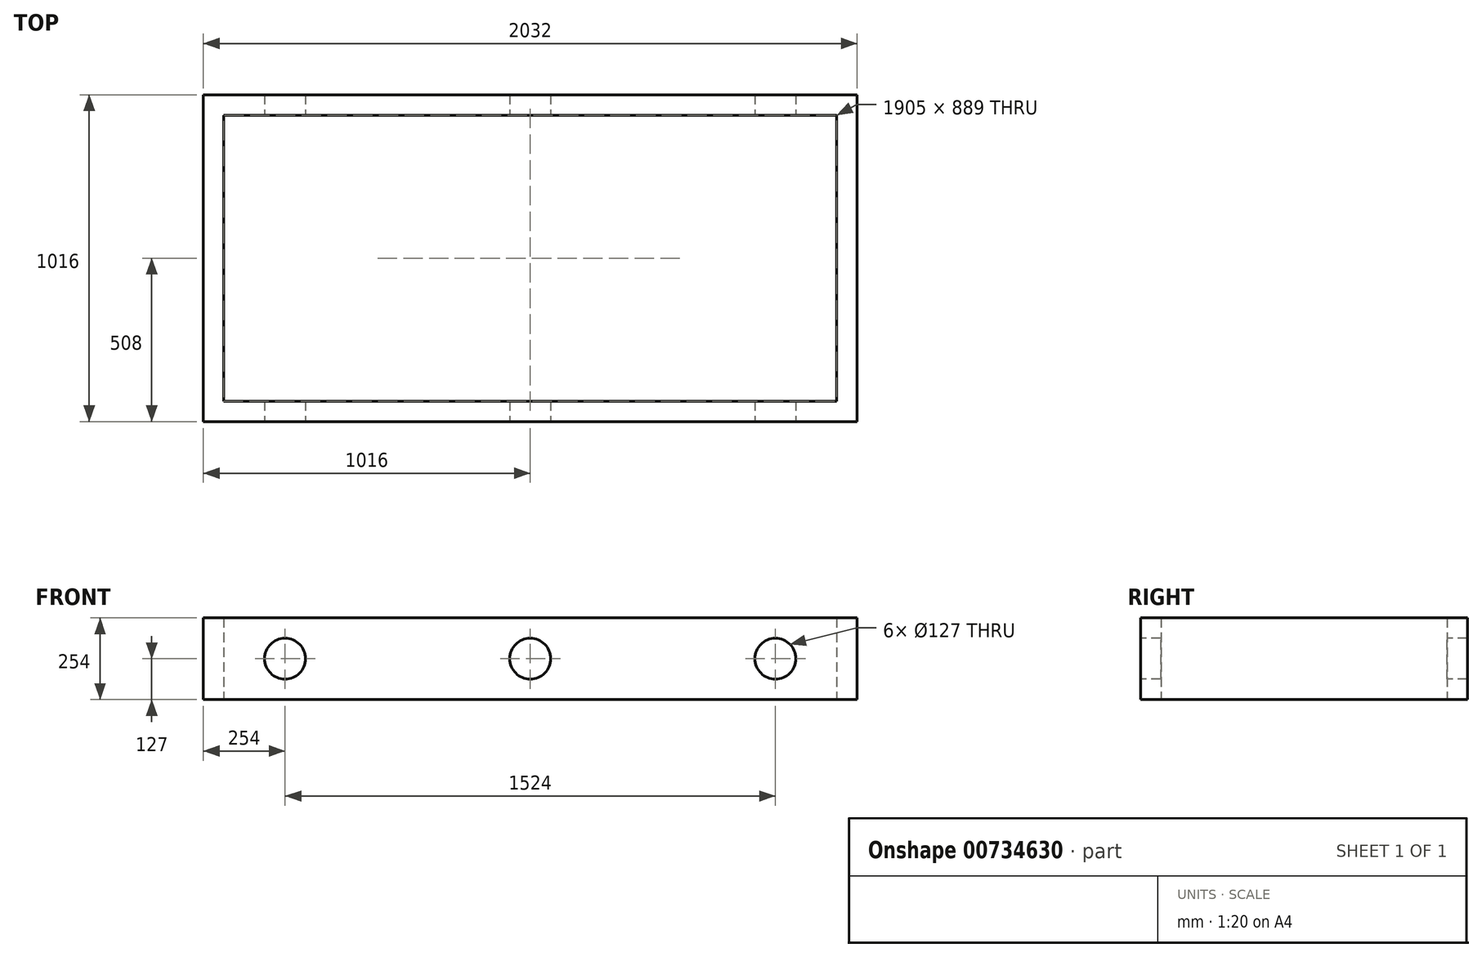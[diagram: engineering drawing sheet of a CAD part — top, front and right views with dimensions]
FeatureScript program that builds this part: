
annotation { "Feature Type Name" : "Feature", "Feature Type Description" : "" }
export const myFeature = defineFeature(function(context is Context, id is Id, definition is map)
    precondition{}
    {
        {
            var Q0;
            Q0=qCreatedBy(makeId("Top.planeOp"),FACE);
            var sketch = newSketch(context, id + "F0", { "sketchPlane" : qUnion([Q0])});
            skLineSegment(sketch, "E0.bottom", {"start": v(1016, -508) * mm, "end": v(-1016, -508) * mm});
            skLineSegment(sketch, "E0.top", {"start": v(1016, 508) * mm, "end": v(-1016, 508) * mm});
            skLineSegment(sketch, "E0.left", {"start": v(1016, -508) * mm, "end": v(1016, 508) * mm});
            skLineSegment(sketch, "E0.right", {"start": v(-1016, -508) * mm, "end": v(-1016, 508) * mm});
            skPoint(sketch, "E0.middle", {"position": v(0, 0) * mm});
            skLineSegment(sketch, "E1.0", {"start": v(952.5, 444.5) * mm, "end": v(-952.5, 444.5) * mm});
            skLineSegment(sketch, "E1.1", {"start": v(952.5, -444.5) * mm, "end": v(952.5, 444.5) * mm});
            skLineSegment(sketch, "E1.2", {"start": v(952.5, -444.5) * mm, "end": v(-952.5, -444.5) * mm});
            skLineSegment(sketch, "E1.3", {"start": v(-952.5, -444.5) * mm, "end": v(-952.5, 444.5) * mm});
            skSolve(sketch);
        }
        {
            var Q0;
            Q0=makeQuery(id+"F0.imprint","IMPRINT",FACE,{"disambiguationData":[TD([[makeQuery(id+"F0.imprint","IMPRINT",EDGE,{"derivedFrom":sQuery(id+"F0.wireOp",EDGE,"E0.bottom")}),-1.0]])]});
            extrude(context, id + "F1", {"entities" : qUnion([Q0]), "depth" : 254 * mm, "offsetDistance" : 25.4 * mm});
        }
        {
            var Q0;
            Q0=makeQuery(id+"F1.opExtrude","SWEPT_FACE",FACE,{"disambiguationData":[OSD([sQuery(id+"F0.wireOp",EDGE,"E0.bottom")])]});
            var sketch = newSketch(context, id + "F2", { "sketchPlane" : qUnion([Q0])});
            skLineSegment(sketch, "E2", {"start": v(-762, 127) * mm, "end": v(762, 127) * mm, "construction": true});
            skCircle(sketch, "E3", {"center": v(-762, 127) * mm, "radius": 63.5 * mm});
            skCircle(sketch, "E4", {"center": v(0, 127) * mm, "radius": 63.5 * mm});
            skCircle(sketch, "E5", {"center": v(762, 127) * mm, "radius": 63.5 * mm});
            skSolve(sketch);
        }
        {
            var Q0;
            Q0=makeQuery(id+"F2.imprint","IMPRINT",FACE,{"disambiguationData":[TD([[makeQuery(id+"F2.imprint","IMPRINT",EDGE,{"derivedFrom":sQuery(id+"F2.wireOp",EDGE,"E4")}),1.0]])]});
            var Q1;
            Q1=makeQuery(id+"F2.imprint","IMPRINT",FACE,{"disambiguationData":[TD([[makeQuery(id+"F2.imprint","IMPRINT",EDGE,{"derivedFrom":sQuery(id+"F2.wireOp",EDGE,"E5")}),1.0]])]});
            var Q2;
            Q2=makeQuery(id+"F2.imprint","IMPRINT",FACE,{"disambiguationData":[TD([[makeQuery(id+"F2.imprint","IMPRINT",EDGE,{"derivedFrom":sQuery(id+"F2.wireOp",EDGE,"E3")}),1.0]])]});
            extrude(context, id + "F3", {"entities" : qUnion([Q0, Q1, Q2]), "operationType" : NewBodyOperationType.REMOVE, "oppositeDirection" : true, "depth" : 1295.4 * mm, "offsetDistance" : 25.4 * mm});
        }
    });
